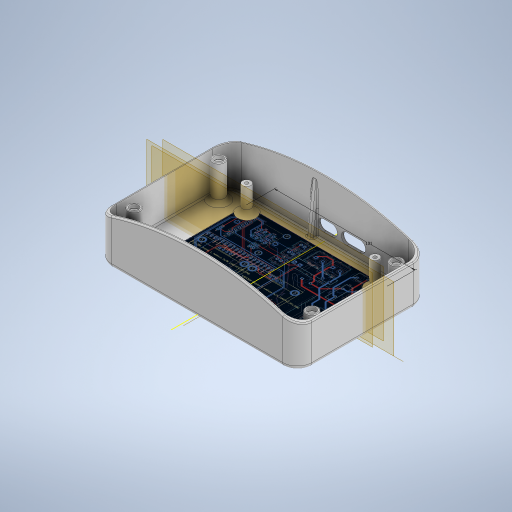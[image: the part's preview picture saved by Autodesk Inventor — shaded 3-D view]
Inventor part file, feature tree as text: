
AUTODESK INVENTOR PART (.ipt)
format: ipt  version: 2024 (Build 280153000, 153)  size: 966,656 bytes
history: native  units: mm
features: sketch x14, extrude x12, fillet x11, projected_geometry x5, mirror x2, other x2, plane x1
ambient origin geometry x8: Origin, YZ Plane, XZ Plane, XY Plane, X Axis, Y Axis, Z Axis, Center Point
bodies: Solid1 (feature_tree)
feature tree (47):
  extrude  "Extrusion1"  Depth=93.65mm
  extrude  "Extrusion2"  Depth=140.55mm
  fillet  "Fillet1"  Radius=90.25mm
  extrude  "Extrusion3"  Depth=10.5mm
  fillet  "Fillet2"  Radius=13.3mm
  fillet  "Fillet3"  Radius=50.0mm
  fillet  "Fillet4"  Radius=3.0mm
  extrude  "Extrusion4"  Depth=1.0mm
  extrude  "Extrusion5"  Depth=25.542mm TaperAngle=0.0deg
  extrude  "Extrusion6"  Depth=5.0mm TaperAngle=0.0deg
  mirror  "Mirror1"
  fillet  "Fillet5"  Radius=6.0mm
  fillet  "Fillet6"  Radius=2.57mm
  plane  "Work Plane1"
  mirror  "Mirror3"
  sketch  "Sketch9"  dims[d26=8.2mm d27=3.0mm]
  sketch  "Sketch10"  dims[d28=1.0mm d29=42.0mm d31=27.341709mm]
  fillet  "Fillet7"  Radius=14.4mm
  extrude  "Extrusion9"  Depth=3.0mm
  extrude  "Extrusion10"  Depth=42.0mm
  other  "screws"
  fillet  "Fillet10"  Radius=27.341709mm
  extrude  "Extrusion11"  Depth=0.5mm
  fillet  "Fillet11"  Radius=101.0mm
  extrude  "Extrusion12"  Depth=18.5mm TaperAngle=0.0deg
  extrude  "Extrusion13"  Depth=10.0mm TaperAngle=0.0deg
  fillet  "Fillet12"  [1 undecoded]
  extrude  "Extrusion14"  Depth=6.0mm
  fillet  "Fillet13"  Radius=2.4mm
  sketch  "Sketch1"  dims[d0=143.95mm d1=93.65mm]
  sketch  "Sketch2"  dims[d2=2.0mm d3=0.0mm d4=140.55mm d5=90.25mm]
  sketch  "Sketch3"  dims[d6=40.0mm d7=0.0mm d8=10.5mm d9=13.3mm d10=50.0mm d11=0.0mm d12=3.0mm]
  sketch  "Sketch5"  dims[d13=1.0mm d14=1.0mm]
  sketch  "Sketch6"  dims[d15=8.5mm d17=25.542mm d18=0.0mm]
  sketch  "Sketch7"  dims[d19=3.47mm d20=5.0mm d21=0.0mm d22=6.0mm d23=2.57mm d24=0.0mm d25=14.4mm]
  other  "Image4"
  sketch  "Sketch14"  dims[d33=-2.1mm d68=0.5mm d123=101.0mm]
  sketch  "Sketch15"  dims[d129=6.0mm d130=18.5mm d131=0.0mm]
  projected_geometry  "Projected Loop1"
  projected_geometry  "Projected Loop2"
  projected_geometry  "Projected Loop3"
  sketch  "Sketch16"  dims[d132=2.4mm d133=10.0mm d134=0.0mm d136=-7.75mm]
  sketch  "Sketch17"  dims[d137=6.0mm d138=6.0mm d139=2.4mm]
  sketch  "Sketch18"  dims[d140=2.4mm]
  projected_geometry  "Projected Loop4"
  projected_geometry  "Projected Loop5"
  sketch  "Sketch19"  dims[d141=2.4mm d142=4.0mm d143=4.0mm d144=43.0mm d145=34.0mm d146=8.0mm d147=18.5mm d148=0.0mm d149=4.0mm d150=4.0mm d151=4.0mm d152=35.0mm d153=0.0mm d154=35.0mm d155=0.0mm d156=1.0mm d157=3.0mm d158=0.0mm d159=0.0mm d160=4.0mm]
note: 1 required parameter value undecoded (feature->parameter linkage not recoverable at this tier; creation-order binding heuristic only, values carry confidence <= 0.55)
